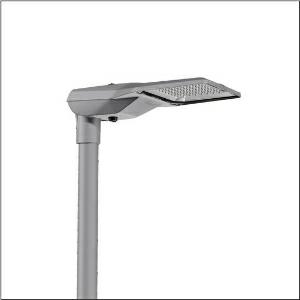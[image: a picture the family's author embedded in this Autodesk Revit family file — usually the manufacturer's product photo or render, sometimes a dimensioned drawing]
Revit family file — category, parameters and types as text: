
# Revit family: streetlight_sl_21_iq_midi___st1_0a_5xe3d41y08mb_a031
name_source: partatom
category: Lighting Fixtures
units: mm (PartAtom-declared; Revit-internal decimal feet)

## family parameters
Cut with Voids When Loaded = No
Host = Face
Light Source = No
Part Type = Normal
Room Calculation Point = No
Round Connector Dimension = Use Diameter
Shared = No

## types (1)
- --- (1 x LED, 18980 lm, 129.3 W, 4000K)
    Apparent Load = 129 VA
    CIE Flux Codes = 37 72 97 100 100
    Color Rendering = 70
    Color Temperature = 4000K
    Default Elevation = 1800 mm
    Description = Streetlight SL 21 iQ midi, mast luminaire, primary light control with lens, of PMMA, primary optical cover: cover, of toughened safety glass, transparent, light distribution: ST1.0a, light emission: direct distribution, primary light characteristic: asymmetric, installation type: post-top, side-entry, LED, High Power LED, rated luminous flux: 18.980lm, luminous efficacy: 147lm/W, light colour: 740, colour temperature: 4000K, control gear: iQ-Street Remote, D4i with power reduction, control: pre-setting: logarithmic dimming characteristic, Street-Remote, Auto-Match, Temp-Guard, Lumen-Switch, Night-Set, Smart-Wire, Light-Fading, Desk-Remote (wireless, voltage-free reading and setting of iQ features in the workshop via application-optimized NFC function/RFID function), optimised constant luminous flux control (CLO 2.0), mains connection: 230..240V, AC, 50/60Hz, start of lifetime: 129W, end of service life: 142W, reduction: 56W, luminaire housing, of diecast aluminium, powder-coated, SITECO metallic grey (DB 702S), corrosivity category C5 high according to DIN EN ISO 12944, please order mast flange separately, inclination adjustable: 0°, 5°, 10°, 15°, sealing non-destructively replaceable, multi-level sealing system, length: 644mm, width: 335mm, height: 110mm, mast flange for spigot size: 42mm (side-entry): 5XC10008XM4, 60/48mm (side-entry/post-top): 5XC10108XM2, 76/60mm (side-entry/post-top): 5XC10108XM1, mounting height: 4..8m, Smart Interface below and above, protection rating (complete): IP66, insulation class (complete): insulation class II (safety insulation), certification: CE, ENEC, ENEC+, VDE, impact resistance: IK10, permissible operating ambient temperature for outdoor applications: -40..+50°C, standard-compliant lighting for roads and squares, packaging unit: 1 piece

Light Distribution: ST1.0a
    Height = 111 mm
    Lamp = 1 x LED
    Lamp Light Flux = 18980 lm
    Lamp Power = 129.3 W
    Lamp count = 1
    Length = 644 mm
    Luminous efficacy = 147 lm/W
    Manufacturer = Siteco
    ModVariant = No
    Model = 5XE3D41Y08MB
    Number of Poles = 1
    OnlyDefault = Yes
    Power Factor = 1
    Product Name = Streetlight SL 21 iQ midi | ST1.0a
    Product group = mast luminaire | pylon top
    ProductGroupID = 6100
    Protection Class = Protection class II
    Protection Degree = IP 66
    RLX_Detail_Level = 1
    RLX_Emergency_Light_Flux = 0 lm
    RLX_Emergency_Type = 0
    RLX_Emergency_Type_DB = No
    RlxData = <blob elided: 91101 chars, md5=a37193c8>
    Socket = socket
    Standby Power = 0 W
    System Light Flux = 18980 lm
    System Power = 129 W
    Type Comments = factory setting: luminous flux: 100 % | dim-lin: 254 | 672 mA
    Type Image = l_1004304.jpg
    URL = http://relux.com
    VarID = @adj_114577
    Voltage = 0 V
    Weight = 0.00 kg
    Width = 336 mm

## geometry (parser evidence)
native form markers: Blend x4, Sweep x10
no freeform markers — native parametric forms only
